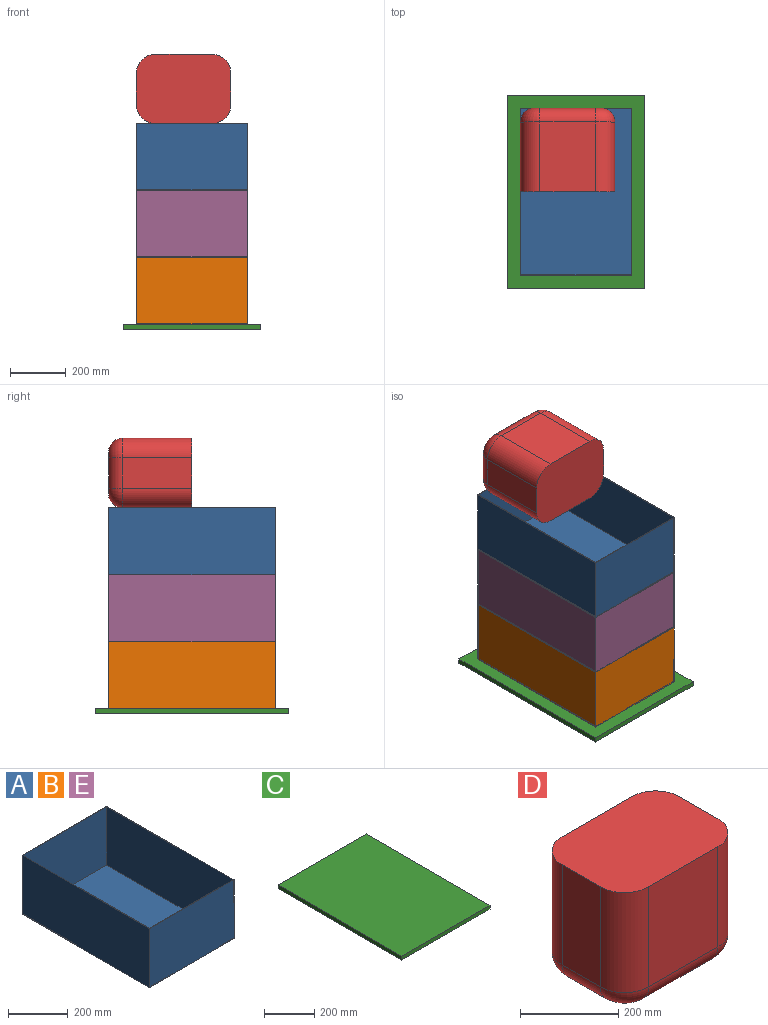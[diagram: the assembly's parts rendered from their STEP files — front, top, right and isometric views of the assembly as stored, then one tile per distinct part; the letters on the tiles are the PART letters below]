
ASSEMBLY  parts=5 mates=1
PART A: 11 faces, bbox 400x600x241 mm
  f0: plane 600x241mm, normal (1,0,0), area 144600mm2, adj f1,f3,f4,f9
  f1: plane 400x241mm, normal (0,1,0), area 96400mm2, adj f0,f2,f4,f9
  f2: plane 600x241mm, normal (-1,0,0), area 144600mm2, adj f1,f3,f4,f9
  f3: plane 400x241mm, normal (0,-1,0), area 96400mm2, adj f0,f2,f4,f9
  f4: plane 600x400mm, normal (0,0,-1), area 240000mm2, adj f0,f1,f2,f3
  f5: plane 596x238mm, normal (-1,0,0), area 141848mm2, adj f6,f8,f9,f10
  f6: plane 396x238mm, normal (0,1,0), area 94248mm2, adj f5,f7,f9,f10
  f7: plane 596x238mm, normal (1,0,0), area 141848mm2, adj f6,f8,f9,f10
  f8: plane 396x238mm, normal (0,-1,0), area 94248mm2, adj f5,f7,f9,f10
  f9: plane 600x400mm, normal (0,0,1), area 3984mm2, adj f0,f1,f2,f3,f5,f6,f7,f8
  f10: plane 596x396mm, normal (0,0,1), area 236016mm2, adj f5,f6,f7,f8
PART B: same geometry as A
PART C: 6 faces, bbox 495x695x18 mm
  f0: plane 695x18mm, normal (1,0,0), area 12510mm2, adj f1,f3,f4,f5
  f1: plane 495x18mm, normal (0,1,0), area 8910mm2, adj f0,f2,f4,f5
  f2: plane 695x18mm, normal (-1,0,0), area 12510mm2, adj f1,f3,f4,f5
  f3: plane 495x18mm, normal (0,-1,0), area 8910mm2, adj f0,f2,f4,f5
  f4: plane 695x495mm, normal (0,0,1), area 344025mm2, adj f0,f1,f2,f3
  f5: plane 695x495mm, normal (0,0,-1), area 344025mm2, adj f0,f1,f2,f3
PART D: 18 faces, bbox 340x250x300 mm
  f0: plane 250x110mm, normal (1,0,0), area 27500mm2, adj f4,f6,f9,f16
  f1: plane 250x200mm, normal (0,1,0), area 50000mm2, adj f4,f6,f7,f15
  f2: plane 250x110mm, normal (-1,0,0), area 27500mm2, adj f4,f7,f8,f11
  f3: plane 250x200mm, normal (0,-1,0), area 50000mm2, adj f4,f8,f9,f12
  f4: plane 340x250mm, normal (0,0,1), area 80793.8mm2, adj f0,f1,f2,f3,f6,f7,f8,f9
  f5: plane 240x150mm, normal (0,0,-1), area 35656.6mm2, adj f10,f11,f12,f13,f14,f15,f16,f17
  f6: cylinder r=70mm len=250mm, axis (0,0,1), area 27488.9mm2, adj f0,f1,f4,f17
  f7: cylinder r=70mm len=250mm, axis (0,0,-1), area 27488.9mm2, adj f1,f2,f4,f13
  f8: cylinder r=70mm len=250mm, axis (0,0,1), area 27488.9mm2, adj f2,f3,f4,f10
  f9: cylinder r=70mm len=250mm, axis (0,0,-1), area 27488.9mm2, adj f0,f3,f4,f14
  f10: torus R=20mm, axis (0,0,1), area 6394.4mm2, adj f5,f8,f11,f12
  f11: cylinder r=50mm len=110mm, axis (0,-1,0), area 8639.4mm2, adj f2,f5,f10,f13
  f12: cylinder r=50mm len=200mm, axis (1,0,0), area 15708mm2, adj f3,f5,f10,f14
  f13: torus R=20mm, axis (0,0,1), area 6394.4mm2, adj f5,f7,f11,f15
  f14: torus R=20mm, axis (0,0,1), area 6394.4mm2, adj f5,f9,f12,f16
  f15: cylinder r=50mm len=200mm, axis (-1,0,0), area 15708mm2, adj f1,f5,f13,f17
  f16: cylinder r=50mm len=110mm, axis (0,1,0), area 8639.4mm2, adj f0,f5,f14,f17
  f17: torus R=20mm, axis (0,0,1), area 6394.4mm2, adj f5,f6,f15,f16
PART E: same geometry as A
PLACE A t=(0,0,482)mm
PLACE B at identity
PLACE C t=(0,0,-18)mm
PLACE D rot(axis=(1,0,0),90deg) t=(-30,300,848)mm
PLACE E t=(0,0,241)mm
MATE fastened B.f4 <-> C.f4  axis (0,0,-1) through (0,0,0)mm
